# Revit family: DBLTD_Kwickscreen_PrvcyScrnSym_Air
name_source: partatom
category: Furniture
units: mm (PartAtom-declared; Revit-internal decimal feet)

## family parameters
Always vertical = Yes
Cut with Voids When Loaded = No
OmniClass Number = 23.40.20.00
OmniClass Title = General Furniture and Specialties
Room Calculation Point = No
Shared = No
Work Plane-Based = No

## types (2) — shared parameters
Assembly Code = E2020200
AssetType = Movable
BIMObjectName = Kwickscreen_PrvcyScrnSym_Kwickscreen
Category = Pr_40_30_20_65:Privacy screens
Color = Defined by material specified
DurationUnit = Years
ExpectedLife = 10
Features = KwickScreens is a portable retractable partitioning system that can flexibly divide up any open plan space, to create private work areas, ad-hoc meeting rooms and event spaces
Finish = Silver anodized Aluminium, but can be powder coated to any colour, and the printed inner panels can be printed with any design
FreeStanding = No
IfcExportAs = IfcFurnishingElementType
IfcExportType = SCREEN
Keynote = Pr_40_30_20_65
MainColor = Defined by material specified
Manufacturer = Kwickscreen
ManufacturerAddressUK = Unit D, Apsley Centre, Apsley Way, London, NW2 7LZ
ManufacturerName = Kwickscreen
ManufacturerURL = http://www.kwickscreen.com
Material = Extruded Aluminium body, Polyester film inner screen with nylon zips, Sheet metal bases and caps
Model = KSAir
ModelNumber = KSAir
NBSDescription = Privacy screen system
NBSReference = 25-05-60/165
Name = PrvcyScrnSym_Kwickscreen_Kwickscreen
NominalHeight = 1905 mm  [stored 6.25 ft]
NominalLength = 433 mm
NominalWidth = 512 mm  [stored 1.67979 ft]
ProductInformation = http://www.kwickscreen.com
ReplacementCost = 0.00
Shape = Vertical Cylinder
Size = W 512mm x D 433 - 3350mm x H 1905mm
URL = www.kwickscreen.com
Uniclass2015Description = Privacy screens
Uniclass2015Reference = Pr_40_30_20_65
Uniclass2015Version = Products v1.3
Version = 1
WallMounted = Yes
WarrantyDescription = Our product quality and reliability is exceptionally high enabling us to provide a minimum 5 year warranty for normal use on all our products
WarrantyDurationLabor = 5
WarrantyDurationParts = 5
WarrantyDurationUnit = Years
zero-valued in all types: Cost

## per-type parameters (varying)
| type | Description | FlatBrackets | ModelReference | StandardBrackets | Type Comments |
| Wall Mounted Screen with Flat Brackets | Portable retractable partition screen with Flat Brackets | Yes | Portable retractable partition screen with Flat Brackets | No | Portable retractable partition screen with Flat Brackets |
| Wall Mounted Screen with Standard Brackets | Portable retractable partition screen with Standard Brackets | No | Portable retractable partition screen with Standard Brackets | Yes | Portable retractable partition screen with Standard Brackets |

note: [stored X ft] marks values corroborated as IEEE doubles in the binary element streams (Revit-internal decimal feet)

## geometry (parser evidence)
native form markers: Revolve x2, Sweep x24
no freeform markers — native parametric forms only
